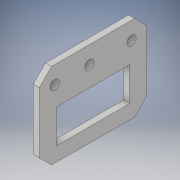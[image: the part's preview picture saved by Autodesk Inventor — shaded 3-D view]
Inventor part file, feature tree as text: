
AUTODESK INVENTOR PART (.ipt)
format: ipt  version: 2017 (Build 210142000, 142)  size: 121,344 bytes
history: native  units: in
note: dims shown in document units (in); Inventor stores cm internally (conversion verified against a paired STEP export)
features: extrude x1, chamfer x1, sketch x1
ambient origin geometry x8: Origin, YZ Plane, XZ Plane, XY Plane, X Axis, Y Axis, Z Axis, Center Point
bodies: Solid1 (feature_tree)
feature tree (3):
  extrude  "Extrusion1"  Depth=1.76in
  chamfer  "Chamfer1"  Distance=0.152in
  sketch  "Sketch1"  dims[d0=1.4in d1=1.76in d2=0.152in d3=0.152in d4=0.152in d5=0.251in d6=0.251in d7=0.286in d8=0.286in d9=0.286in d10=0.55in d11=1.2in d12=0.616in d13=0.28in d14=0.1in d15=0.0in d16=0.2in d17=0.125in d18=45.0deg]
